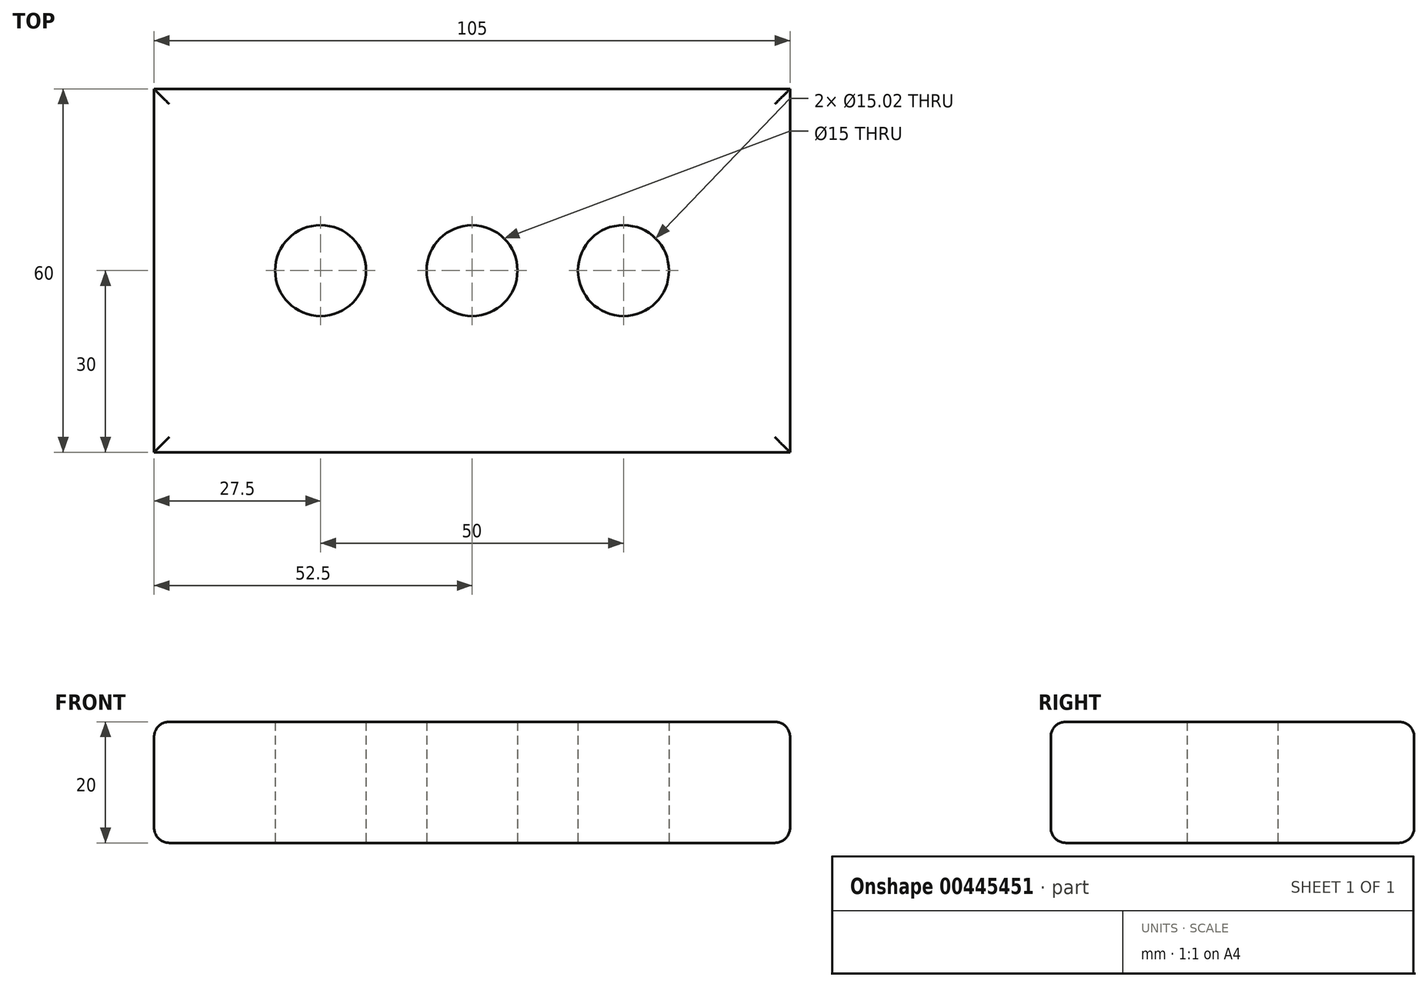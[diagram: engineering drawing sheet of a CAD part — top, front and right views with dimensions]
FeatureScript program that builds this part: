
annotation { "Feature Type Name" : "Feature", "Feature Type Description" : "" }
export const myFeature = defineFeature(function(context is Context, id is Id, definition is map)
    precondition{}
    {
        {
            var Q0;
            Q0=qCreatedBy(makeId("Top.planeOp"),FACE);
            var sketch = newSketch(context, id + "F0", { "sketchPlane" : qUnion([Q0])});
            skLineSegment(sketch, "E0.bottom", {"start": v(52.5, 30) * mm, "end": v(-52.5, 30) * mm});
            skLineSegment(sketch, "E0.top", {"start": v(52.5, -30) * mm, "end": v(-52.5, -30) * mm});
            skLineSegment(sketch, "E0.left", {"start": v(52.5, 30) * mm, "end": v(52.5, -30) * mm});
            skLineSegment(sketch, "E0.right", {"start": v(-52.5, 30) * mm, "end": v(-52.5, -30) * mm});
            skPoint(sketch, "E0.middle", {"position": v(0, 0) * mm});
            skSolve(sketch);
        }
        {
            var Q0;
            Q0=makeQuery(id+"F0.imprint","IMPRINT",FACE,{"disambiguationData":[TD([[makeQuery(id+"F0.imprint","IMPRINT",EDGE,{"derivedFrom":sQuery(id+"F0.wireOp",EDGE,"E0.bottom")}),1.0]])]});
            extrude(context, id + "F1", {"entities" : qUnion([Q0]), "depth" : 20 * mm});
        }
        {
            var Q0;
            Q0=qCreatedBy(makeId("Top.planeOp"),FACE);
            var sketch = newSketch(context, id + "F2", { "sketchPlane" : qUnion([Q0])});
            skCircle(sketch, "E1", {"center": v(0, 0) * mm, "radius": 7.5 * mm});
            skCircle(sketch, "E2", {"center": v(-25, 0) * mm, "radius": 7.5 * mm});
            skCircle(sketch, "E3", {"center": v(25, 0) * mm, "radius": 7.5 * mm});
            skSolve(sketch);
        }
        {
            var Q0;
            Q0 = qSketchRegion(id + "F2", true);
            extrude(context, id + "F3", {"entities" : qUnion([Q0]), "operationType" : NewBodyOperationType.REMOVE, "endBound" : BoundingType.THROUGH_ALL, "depth" : 25 * mm});
        }
        {
            var Q0;
            Q0=makeQuery(id+"F1.opExtrude","CAP_EDGE",EDGE,{"disambiguationData":[OSD([sQuery(id+"F0.wireOp",EDGE,"E0.bottom")])],"isStart":true});
            var Q1;
            Q1=makeQuery(id+"F1.opExtrude","CAP_EDGE",EDGE,{"disambiguationData":[OSD([sQuery(id+"F0.wireOp",EDGE,"E0.left")])],"isStart":true});
            var Q2;
            Q2=makeQuery(id+"F1.opExtrude","CAP_EDGE",EDGE,{"disambiguationData":[OSD([sQuery(id+"F0.wireOp",EDGE,"E0.top")])],"isStart":true});
            var Q3;
            Q3=makeQuery(id+"F1.opExtrude","CAP_EDGE",EDGE,{"disambiguationData":[OSD([sQuery(id+"F0.wireOp",EDGE,"E0.right")])],"isStart":true});
            var Q4;
            Q4=makeQuery(id+"F1.opExtrude","CAP_EDGE",EDGE,{"disambiguationData":[OSD([sQuery(id+"F0.wireOp",EDGE,"E0.bottom")])],"isStart":false});
            var Q5;
            Q5=makeQuery(id+"F1.opExtrude","CAP_EDGE",EDGE,{"disambiguationData":[OSD([sQuery(id+"F0.wireOp",EDGE,"E0.left")])],"isStart":false});
            var Q6;
            Q6=makeQuery(id+"F1.opExtrude","CAP_EDGE",EDGE,{"disambiguationData":[OSD([sQuery(id+"F0.wireOp",EDGE,"E0.top")])],"isStart":false});
            var Q7;
            Q7=makeQuery(id+"F1.opExtrude","CAP_EDGE",EDGE,{"disambiguationData":[OSD([sQuery(id+"F0.wireOp",EDGE,"E0.right")])],"isStart":false});
            fillet(context, id + "F4", {"entities" : qUnion([Q0, Q1, Q2, Q3, Q4, Q5, Q6, Q7]), "radius" : 2.5 * mm, "tangentPropagation" : true, "allowEdgeOverflow" : false});
        }
    });
